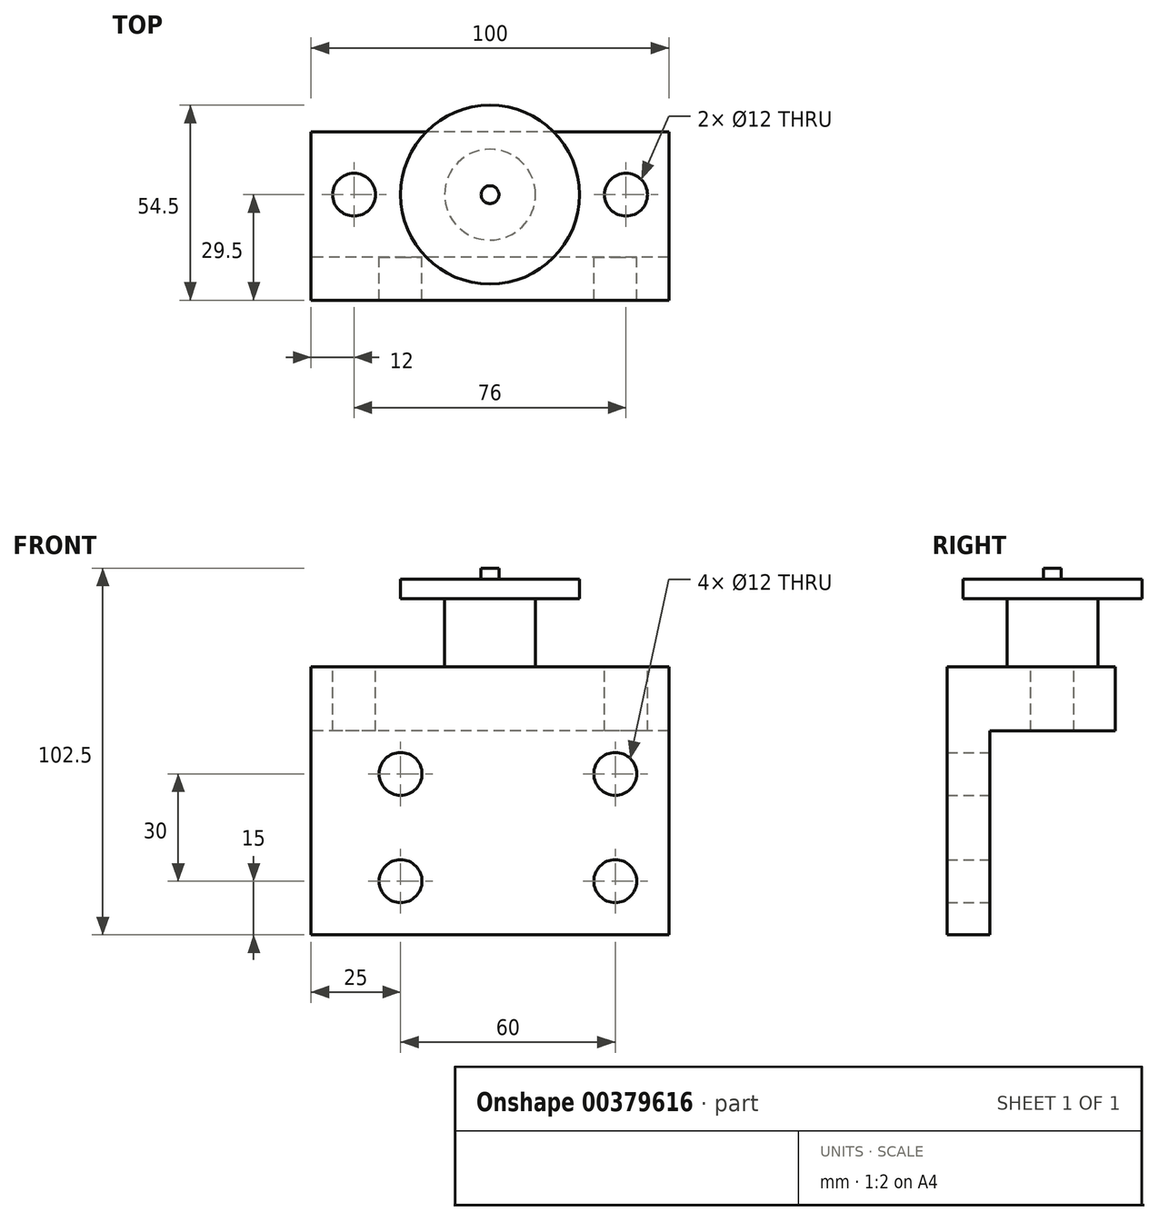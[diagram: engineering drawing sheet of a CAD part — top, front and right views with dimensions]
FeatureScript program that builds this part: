
annotation { "Feature Type Name" : "Feature", "Feature Type Description" : "" }
export const myFeature = defineFeature(function(context is Context, id is Id, definition is map)
    precondition{}
    {
        {
            var Q0;
            Q0=qCreatedBy(makeId("Top.planeOp"),FACE);
            var sketch = newSketch(context, id + "F0", { "sketchPlane" : qUnion([Q0])});
            skLineSegment(sketch, "E0.bottom", {"start": v(50, -17.5) * mm, "end": v(-50, -17.5) * mm});
            skLineSegment(sketch, "E0.top", {"start": v(50, 17.5) * mm, "end": v(-50, 17.5) * mm});
            skLineSegment(sketch, "E0.left", {"start": v(50, -17.5) * mm, "end": v(50, 17.5) * mm});
            skLineSegment(sketch, "E0.right", {"start": v(-50, -17.5) * mm, "end": v(-50, 17.5) * mm});
            skPoint(sketch, "E0.middle", {"position": v(0, 0) * mm});
            skSolve(sketch);
        }
        {
            var Q0;
            Q0=makeQuery(id+"F0.imprint","IMPRINT",FACE,{"disambiguationData":[TD([[makeQuery(id+"F0.imprint","IMPRINT",EDGE,{"derivedFrom":sQuery(id+"F0.wireOp",EDGE,"E0.bottom")}),-1.0]])]});
            extrude(context, id + "F1", {"entities" : qUnion([Q0]), "depth" : -18 * mm});
        }
        {
            var Q0;
            Q0=makeQuery(id+"F1.opExtrude","CAP_FACE",FACE,{"disambiguationData":[OSD([sQuery(id+"F0.wireOp",EDGE,"E0.bottom"),sQuery(id+"F0.wireOp",EDGE,"E0.top"),sQuery(id+"F0.wireOp",EDGE,"E0.left"),sQuery(id+"F0.wireOp",EDGE,"E0.right")])],"isStart":true});
            var sketch = newSketch(context, id + "F2", { "sketchPlane" : qUnion([Q0])});
            skLineSegment(sketch, "E1", {"start": v(50, 0) * mm, "end": v(38, 0) * mm, "construction": true});
            skLineSegment(sketch, "E2", {"start": v(-50, 0) * mm, "end": v(-38, 0) * mm, "construction": true});
            skCircle(sketch, "E3", {"center": v(38, 0) * mm, "radius": 6 * mm});
            skCircle(sketch, "E4", {"center": v(-38, 0) * mm, "radius": 6 * mm});
            skSolve(sketch);
        }
        {
            var Q0;
            Q0=sQuery(id+"F2.wireOp",VERTEX,"E2.end");
            var Q1;
            Q1=sQuery(id+"F2.wireOp",VERTEX,"E3.center");
            var Q2;
            Q2=makeQuery(id+"F1.opExtrude","SWEPT_BODY",BODY,{"disambiguationData":[OSD([sQuery(id+"F0.wireOp",EDGE,"E0.bottom"),sQuery(id+"F0.wireOp",EDGE,"E0.top"),sQuery(id+"F0.wireOp",EDGE,"E0.left"),sQuery(id+"F0.wireOp",EDGE,"E0.right")])]});
            hole(context, id + "F3", {"style" : HoleStyle.SIMPLE, "endStyle" : HoleEndStyle.THROUGH, "holeDiameter" : 12 * mm, "isTappedThrough" : true, "tappedDepth" : 12 * mm, "tapClearance" : 3, "locations" : qUnion([Q0, Q1]), "scope" : qUnion([Q2])});
        }
        {
            var Q0;
            Q0=makeQuery(id+"F1.opExtrude","CAP_FACE",FACE,{"disambiguationData":[OSD([sQuery(id+"F0.wireOp",EDGE,"E0.bottom"),sQuery(id+"F0.wireOp",EDGE,"E0.top"),sQuery(id+"F0.wireOp",EDGE,"E0.left"),sQuery(id+"F0.wireOp",EDGE,"E0.right")])],"isStart":true});
            var sketch = newSketch(context, id + "F4", { "sketchPlane" : qUnion([Q0])});
            skCircle(sketch, "E5", {"center": v(0, 0) * mm, "radius": 12.7 * mm});
            skSolve(sketch);
        }
        {
            var Q0;
            Q0=makeQuery(id+"F4.imprint","IMPRINT",FACE,{"disambiguationData":[TD([[makeQuery(id+"F4.imprint","IMPRINT",EDGE,{"derivedFrom":sQuery(id+"F4.wireOp",EDGE,"E5")}),1.0]])]});
            extrude(context, id + "F5", {"entities" : qUnion([Q0]), "operationType" : NewBodyOperationType.ADD, "depth" : 19 * mm});
        }
        {
            var Q0;
            Q0=makeQuery(id+"F5.opExtrude","CAP_FACE",FACE,{"disambiguationData":[OSD([sQuery(id+"F4.wireOp",EDGE,"E5")])],"isStart":false});
            var sketch = newSketch(context, id + "F6", { "sketchPlane" : qUnion([Q0])});
            skCircle(sketch, "E6", {"center": v(0, 0) * mm, "radius": 25 * mm});
            skSolve(sketch);
        }
        {
            var Q0;
            Q0=makeQuery(id+"F6.imprint","IMPRINT",FACE,{"disambiguationData":[TD([[makeQuery(id+"F6.imprint","IMPRINT",EDGE,{"derivedFrom":sQuery(id+"F6.wireOp",EDGE,"E6")}),1.0]])]});
            var Q1;
            Q1=makeQuery(id+"F6.imprint","IMPRINT",FACE,{"disambiguationData":[TD([[makeQuery(id+"F6.imprint","IMPRINT",EDGE,{"derivedFrom":makeQuery(id+"F5.opExtrude","CAP_EDGE",EDGE,{"disambiguationData":[OSD([sQuery(id+"F4.wireOp",EDGE,"E5")])],"isStart":false})}),1.0]])]});
            extrude(context, id + "F7", {"entities" : qUnion([Q0, Q1]), "operationType" : NewBodyOperationType.ADD, "depth" : 5.5 * mm});
        }
        {
            var Q0;
            Q0=makeQuery(id+"F7.opExtrude","CAP_FACE",FACE,{"disambiguationData":[OSD([sQuery(id+"F6.wireOp",EDGE,"E6")])],"isStart":false});
            var sketch = newSketch(context, id + "F8", { "sketchPlane" : qUnion([Q0])});
            skCircle(sketch, "E7", {"center": v(0, 0) * mm, "radius": 2.5 * mm});
            skSolve(sketch);
        }
        {
            var Q0;
            Q0=qSketchRegion(id+"F8",true);
            extrude(context, id + "F9", {"entities" : qUnion([Q0]), "operationType" : NewBodyOperationType.ADD, "depth" : 3 * mm});
        }
        {
            var Q0;
            Q0=makeQuery(id+"F1.opExtrude","SWEPT_FACE",FACE,{"disambiguationData":[OSD([sQuery(id+"F0.wireOp",EDGE,"E0.bottom")])]});
            var sketch = newSketch(context, id + "F10", { "sketchPlane" : qUnion([Q0])});
            skLineSegment(sketch, "E8.bottom", {"start": v(-50, 0) * mm, "end": v(50, 0) * mm});
            skLineSegment(sketch, "E8.top", {"start": v(-50, -75) * mm, "end": v(50, -75) * mm});
            skLineSegment(sketch, "E8.left", {"start": v(-50, 0) * mm, "end": v(-50, -75) * mm});
            skLineSegment(sketch, "E8.right", {"start": v(50, 0) * mm, "end": v(50, -75) * mm});
            skSolve(sketch);
        }
        {
            var Q0;
            {var subQ0=sQuery(id+"F10.wireOp",EDGE,"E8.top");Q0=makeQuery(id+"F10.imprint","IMPRINT",FACE,{"disambiguationData":[TD([[makeQuery(id+"F10.imprint","IMPRINT",EDGE,{"derivedFrom":subQ0}),1.0]])]});}
            var Q1;
            {var subQ0=sQuery(id+"F10.wireOp",EDGE,"E8.bottom");Q1=makeQuery(id+"F10.imprint","IMPRINT",FACE,{"disambiguationData":[TD([[makeQuery(id+"F10.imprint","IMPRINT",EDGE,{"derivedFrom":subQ0}),1.0]])]});}
            extrude(context, id + "F11", {"entities" : qUnion([Q0, Q1]), "operationType" : NewBodyOperationType.ADD, "depth" : 12 * mm});
        }
        {
            var Q0;
            Q0=makeQuery(id+"F11.opExtrude","CAP_FACE",FACE,{"disambiguationData":[OSD([sQuery(id+"F10.wireOp",EDGE,"E8.bottom"),sQuery(id+"F10.wireOp",EDGE,"E8.top"),sQuery(id+"F10.wireOp",EDGE,"E8.left"),sQuery(id+"F10.wireOp",EDGE,"E8.right")])],"isStart":true});
            var sketch = newSketch(context, id + "F12", { "sketchPlane" : qUnion([Q0])});
            skLineSegment(sketch, "E9", {"start": v(-50, -75) * mm, "end": v(-50, -60) * mm, "construction": true});
            skLineSegment(sketch, "E10", {"start": v(-50, -60) * mm, "end": v(-35, -60) * mm, "construction": true});
            skLineSegment(sketch, "E11", {"start": v(-50, -18) * mm, "end": v(-50, -30) * mm, "construction": true});
            skLineSegment(sketch, "E12", {"start": v(-50, -30) * mm, "end": v(-35, -30) * mm, "construction": true});
            skLineSegment(sketch, "E13", {"start": v(-35, -60) * mm, "end": v(-35, -30) * mm, "construction": true});
            skLineSegment(sketch, "E14", {"start": v(50, -75) * mm, "end": v(50, -60) * mm, "construction": true});
            skLineSegment(sketch, "E15", {"start": v(-35, -60) * mm, "end": v(25, -60) * mm, "construction": true});
            skLineSegment(sketch, "E16", {"start": v(-35, -30) * mm, "end": v(25, -30) * mm, "construction": true});
            skSolve(sketch);
        }
        {
            var Q0;
            Q0=sQuery(id+"F12.wireOp",VERTEX,"E13.end");
            var Q1;
            Q1=sQuery(id+"F12.wireOp",VERTEX,"E13.start");
            var Q2;
            Q2=sQuery(id+"F12.wireOp",VERTEX,"xTalogH7-6SUX-YjE4-XHyp-eRCsPLS0GgkF.end");
            var Q3;
            Q3=sQuery(id+"F12.wireOp",VERTEX,"bwlBc64T-aBhr-B5nw-uTOJ-tdVbFX9mHNVS.end");
            var Q4;
            Q4=sQuery(id+"F12.wireOp",VERTEX,"E16.end");
            var Q5;
            Q5=sQuery(id+"F12.wireOp",VERTEX,"E15.end");
            var Q6;
            Q6=makeQuery(id+"F1.opExtrude","SWEPT_BODY",BODY,{"disambiguationData":[OSD([sQuery(id+"F0.wireOp",EDGE,"E0.bottom"),sQuery(id+"F0.wireOp",EDGE,"E0.top"),sQuery(id+"F0.wireOp",EDGE,"E0.left"),sQuery(id+"F0.wireOp",EDGE,"E0.right")])]});
            hole(context, id + "F13", {"style" : HoleStyle.SIMPLE, "endStyle" : HoleEndStyle.THROUGH, "holeDiameter" : 12 * mm, "isTappedThrough" : true, "tappedDepth" : 12 * mm, "tapClearance" : 3, "locations" : qUnion([Q0, Q1, Q2, Q3, Q4, Q5]), "scope" : qUnion([Q6])});
        }
    });
